# Revit family: 9467 Скамейка стальная «Колледж» Хоббика
name_source: partatom
category: Антураж
revit_build: Autodesk Revit 2018 (Build: 20180423_1000(x64)
units: mm (PartAtom-declared; Revit-internal decimal feet)

## family parameters
Всегда вертикально = Да
Источник визуального образа = Геометрия семейства
На основе рабочей плоскости = Нет
Общий = Нет
При загрузке вырезать с полостями = Нет
Точка расчета площади = Нет

## types (6) — shared parameters
URL = https://hobbyka.ru
Артикул товара = Арт. 9467
Высота = 820 мм
Группа модели = Скамейки
Изготовитель = ООО «Хоббика»
Изображение типоразмера = Скамейка стальная «Колледж» Арт 9467.jpg
Материал изделия = Сталь, дерево
Цвет лавки = Дерево
Цвет опор = Сталь
Ширина = 470 мм

## per-type parameters (varying)
| type | Версия 1,2 м | Версия 1,5 м | Версия 1,8 м | Версия 2,0 м (3 опоры) | Версия 2,5 м (3 опоры) | Версия 3,0 м (3 опоры) | Длина | Описание | Средняя опора |
| Версия 1,2 м | Да | Нет | Нет | Нет | Нет | Нет | 1200 мм | Скамейка стальная «Колледж». Версия 1,2 м | Нет |
| Версия 1,5 м | Нет | Да | Нет | Нет | Нет | Нет | 1500 мм | Скамейка стальная «Колледж». Версия 1,5 м | Нет |
| Версия 1,8 м | Нет | Нет | Да | Нет | Нет | Нет | 1800 мм | Скамейка стальная «Колледж». Версия 1,8 м | Нет |
| Версия 2,0 м (3 опоры) | Нет | Нет | Нет | Да | Нет | Нет | 2000 мм | Скамейка стальная «Колледж». Версия 2,0 м (3 опоры) | Да |
| Версия 2,5 м (3 опоры) | Нет | Нет | Нет | Нет | Да | Нет | 2500 мм | Скамейка стальная «Колледж». Версия 2,5 м (3 опоры) | Да |
| Версия 3,0 м (3 опоры) | Нет | Нет | Нет | Нет | Нет | Да | 3000 мм | Скамейка стальная «Колледж». Версия 3,0 м (3 опоры) | Да |
